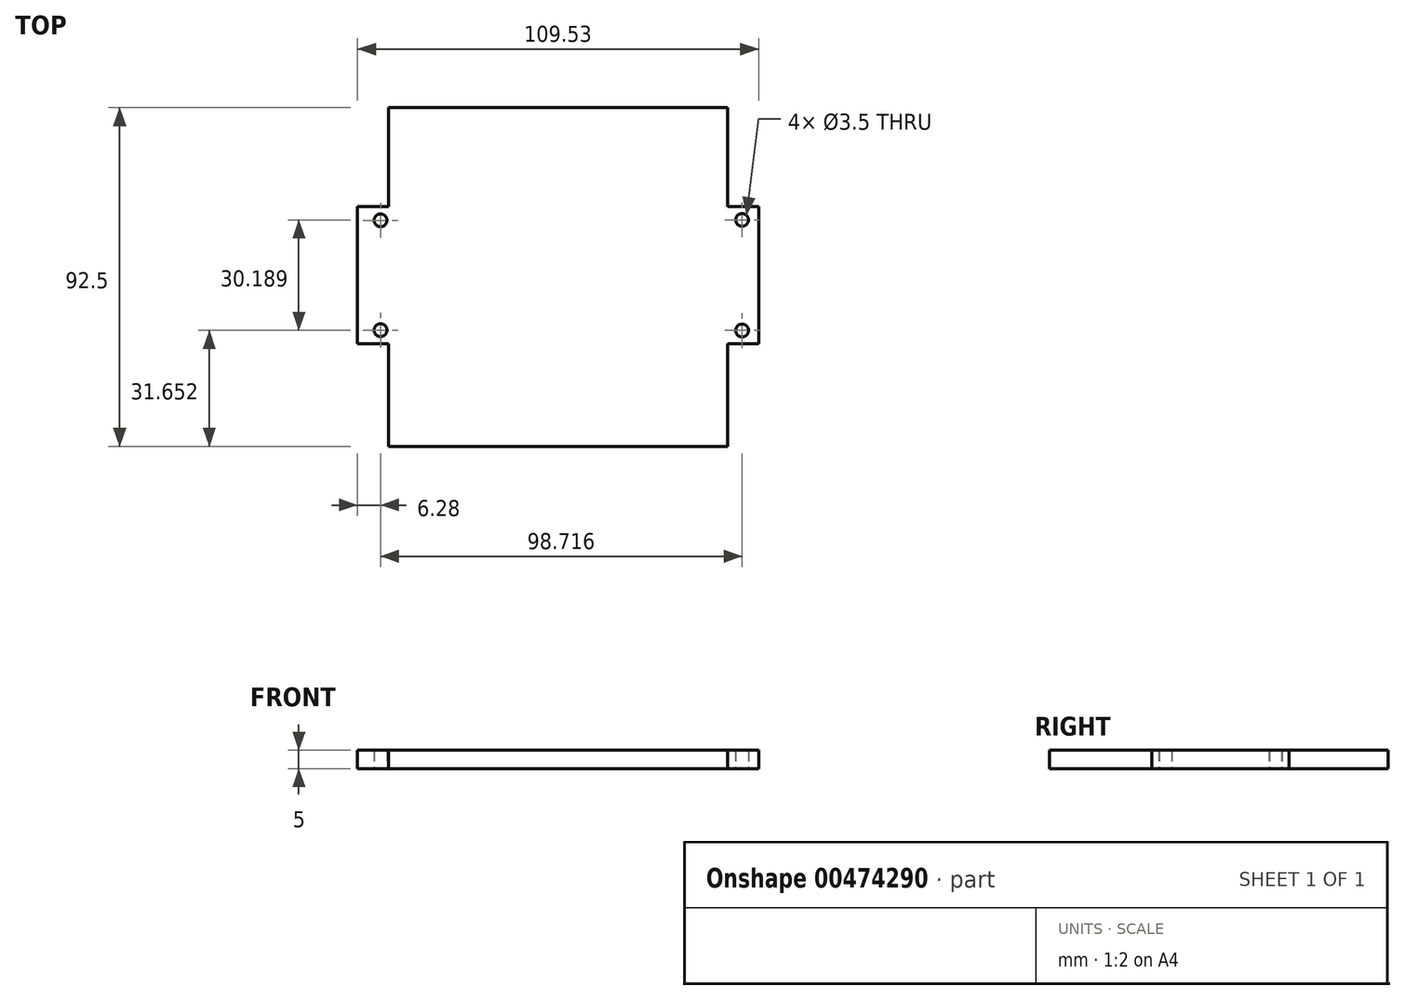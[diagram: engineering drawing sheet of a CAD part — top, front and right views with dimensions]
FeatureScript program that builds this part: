
annotation { "Feature Type Name" : "Feature", "Feature Type Description" : "" }
export const myFeature = defineFeature(function(context is Context, id is Id, definition is map)
    precondition{}
    {
        {
            var Q0;
            Q0=qCreatedBy(makeId("Top.planeOp"),FACE);
            var sketch = newSketch(context, id + "F0", { "sketchPlane" : qUnion([Q0])});
            skLineSegment(sketch, "E0.bottom", {"start": v(-34.72, 69.56) * mm, "end": v(57.78, 69.56) * mm});
            skLineSegment(sketch, "E0.top", {"start": v(-34.72, -22.94) * mm, "end": v(57.78, -22.94) * mm});
            skPoint(sketch, "E1", {"position": v(-34.72, 42.56) * mm});
            skPoint(sketch, "E2", {"position": v(-34.72, 5.06) * mm});
            skPoint(sketch, "E3", {"position": v(57.78, 42.56) * mm});
            skPoint(sketch, "E4", {"position": v(57.78, 5.06) * mm});
            skLineSegment(sketch, "E5", {"start": v(57.78, 42.56) * mm, "end": v(66.3, 42.56) * mm});
            skLineSegment(sketch, "E6", {"start": v(66.3, 42.56) * mm, "end": v(66.3, 5.06) * mm});
            skLineSegment(sketch, "E7", {"start": v(66.3, 5.06) * mm, "end": v(57.78, 5.06) * mm});
            skLineSegment(sketch, "E8", {"start": v(-34.72, 42.56) * mm, "end": v(-43.22, 42.56) * mm});
            skLineSegment(sketch, "E9", {"start": v(-43.22, 42.56) * mm, "end": v(-43.22, 5.06) * mm});
            skLineSegment(sketch, "E10", {"start": v(-43.22, 5.06) * mm, "end": v(-34.72, 5.06) * mm});
            skCircle(sketch, "E11", {"center": v(-36.94, 38.78) * mm, "radius": 1.75 * mm});
            skCircle(sketch, "E12", {"center": v(61.78, 8.71) * mm, "radius": 1.75 * mm});
            skCircle(sketch, "E13", {"center": v(-36.94, 8.78) * mm, "radius": 1.75 * mm});
            skLineSegment(sketch, "E14", {"start": v(-34.72, 42.56) * mm, "end": v(-34.72, 69.56) * mm});
            skLineSegment(sketch, "E15", {"start": v(-34.72, 5.06) * mm, "end": v(-34.72, -22.94) * mm});
            skLineSegment(sketch, "E16", {"start": v(57.78, 42.56) * mm, "end": v(57.78, 69.56) * mm});
            skLineSegment(sketch, "E17", {"start": v(57.78, 5.06) * mm, "end": v(57.78, -22.94) * mm});
            skLineSegment(sketch, "E18", {"start": v(61.78, 5.06) * mm, "end": v(61.78, 8.71) * mm});
            skLineSegment(sketch, "E19", {"start": v(61.78, 8.71) * mm, "end": v(66.3, 8.71) * mm});
            skCircle(sketch, "E20", {"center": v(61.77, 38.9) * mm, "radius": 1.75 * mm});
            skSolve(sketch);
        }
        {
            var Q0;
            Q0 = qSketchRegion(id + "F0", true);
            extrude(context, id + "F1", {"entities" : qUnion([Q0]), "depth" : 5 * mm, "offsetDistance" : 25 * mm});
        }
    });
